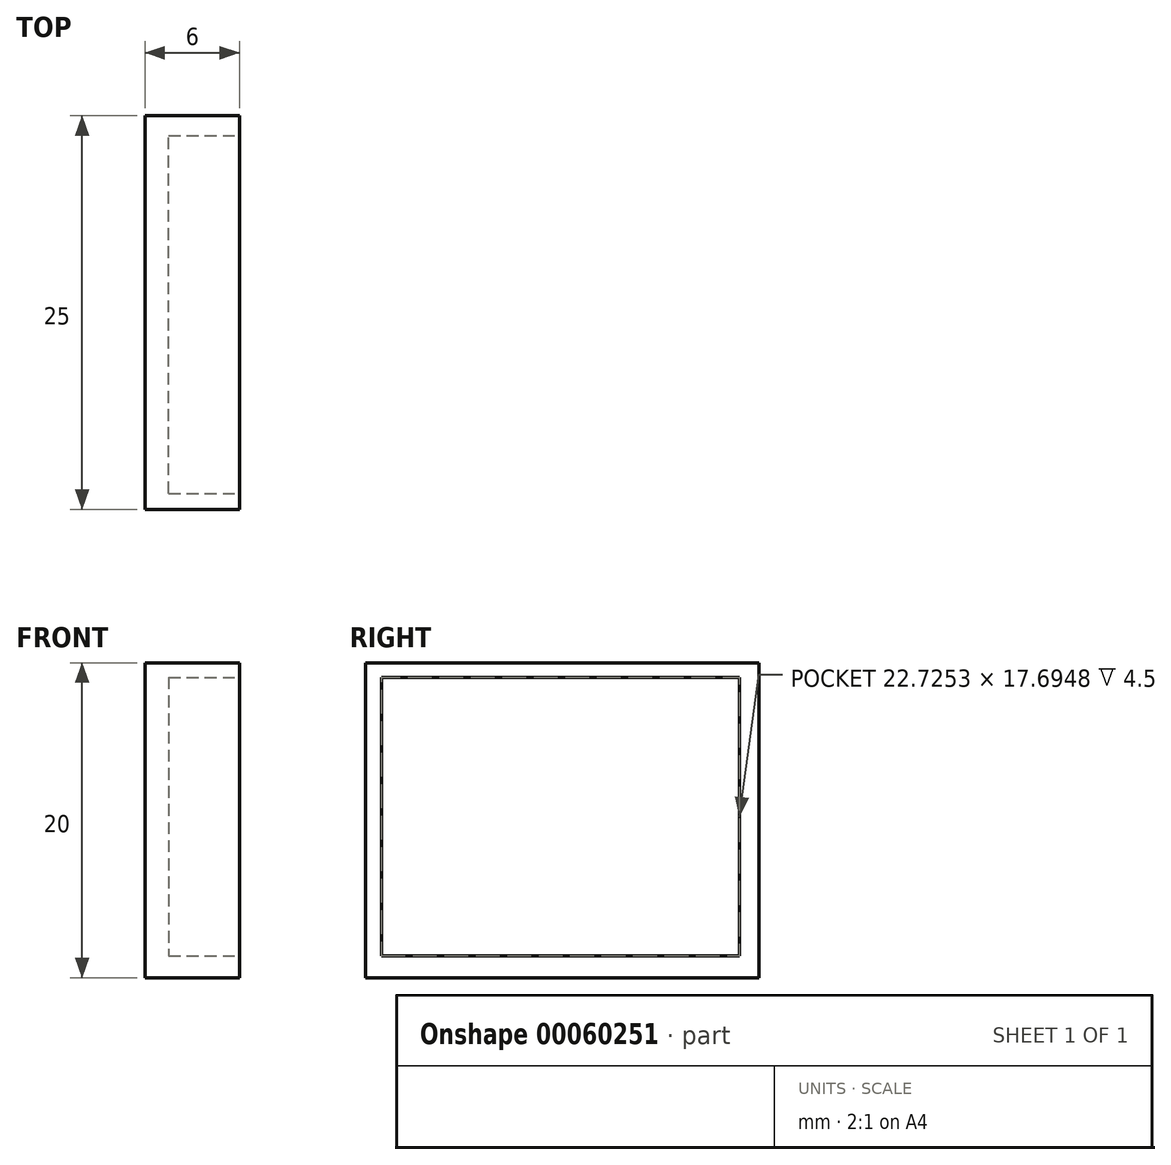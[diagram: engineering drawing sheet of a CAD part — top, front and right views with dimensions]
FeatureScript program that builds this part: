
annotation { "Feature Type Name" : "Feature", "Feature Type Description" : "" }
export const myFeature = defineFeature(function(context is Context, id is Id, definition is map)
    precondition{}
    {
        {
            var Q0;
            Q0=qCreatedBy(makeId("Right.planeOp"),FACE);
            var sketch = newSketch(context, id + "F0", { "sketchPlane" : qUnion([Q0])});
            skLineSegment(sketch, "E0.rect.bottom", {"start": v(12.5, -10) * mm, "end": v(-12.5, -10) * mm});
            skLineSegment(sketch, "E0.rect.top", {"start": v(12.5, 10) * mm, "end": v(-12.5, 10) * mm});
            skLineSegment(sketch, "E0.rect.left", {"start": v(12.5, -10) * mm, "end": v(12.5, 10) * mm});
            skLineSegment(sketch, "E0.rect.right", {"start": v(-12.5, -10) * mm, "end": v(-12.5, 10) * mm});
            skPoint(sketch, "E0.rect.middle", {"position": v(0, 0) * mm});
            skSolve(sketch);
        }
        {
            var Q0;
            Q0 = qSketchRegion(id + "F0", true);
            extrude(context, id + "F1", {"entities" : qUnion([Q0]), "depth" : 6 * mm});
        }
        {
            var Q0;
            Q0=makeQuery(id+"F1.opExtrude","CAP_FACE",FACE,{"disambiguationData":[OSD([sQuery(id+"F0.wireOp",EDGE,"E0.rect.bottom"),sQuery(id+"F0.wireOp",EDGE,"E0.rect.top"),sQuery(id+"F0.wireOp",EDGE,"E0.rect.left"),sQuery(id+"F0.wireOp",EDGE,"E0.rect.right")])],"isStart":false});
            var sketch = newSketch(context, id + "F2", { "sketchPlane" : qUnion([Q0])});
            skLineSegment(sketch, "E1.bottom", {"start": v(-11.48, 9.08) * mm, "end": v(11.24, 9.08) * mm});
            skLineSegment(sketch, "E1.top", {"start": v(-11.48, -8.62) * mm, "end": v(11.24, -8.62) * mm});
            skLineSegment(sketch, "E1.left", {"start": v(-11.48, 9.08) * mm, "end": v(-11.48, -8.62) * mm});
            skLineSegment(sketch, "E1.right", {"start": v(11.24, 9.08) * mm, "end": v(11.24, -8.62) * mm});
            skSolve(sketch);
        }
        {
            var Q0;
            Q0 = qSketchRegion(id + "F2", true);
            extrude(context, id + "F3", {"entities" : qUnion([Q0]), "operationType" : NewBodyOperationType.REMOVE, "oppositeDirection" : true, "depth" : 4.5 * mm});
        }
    });
